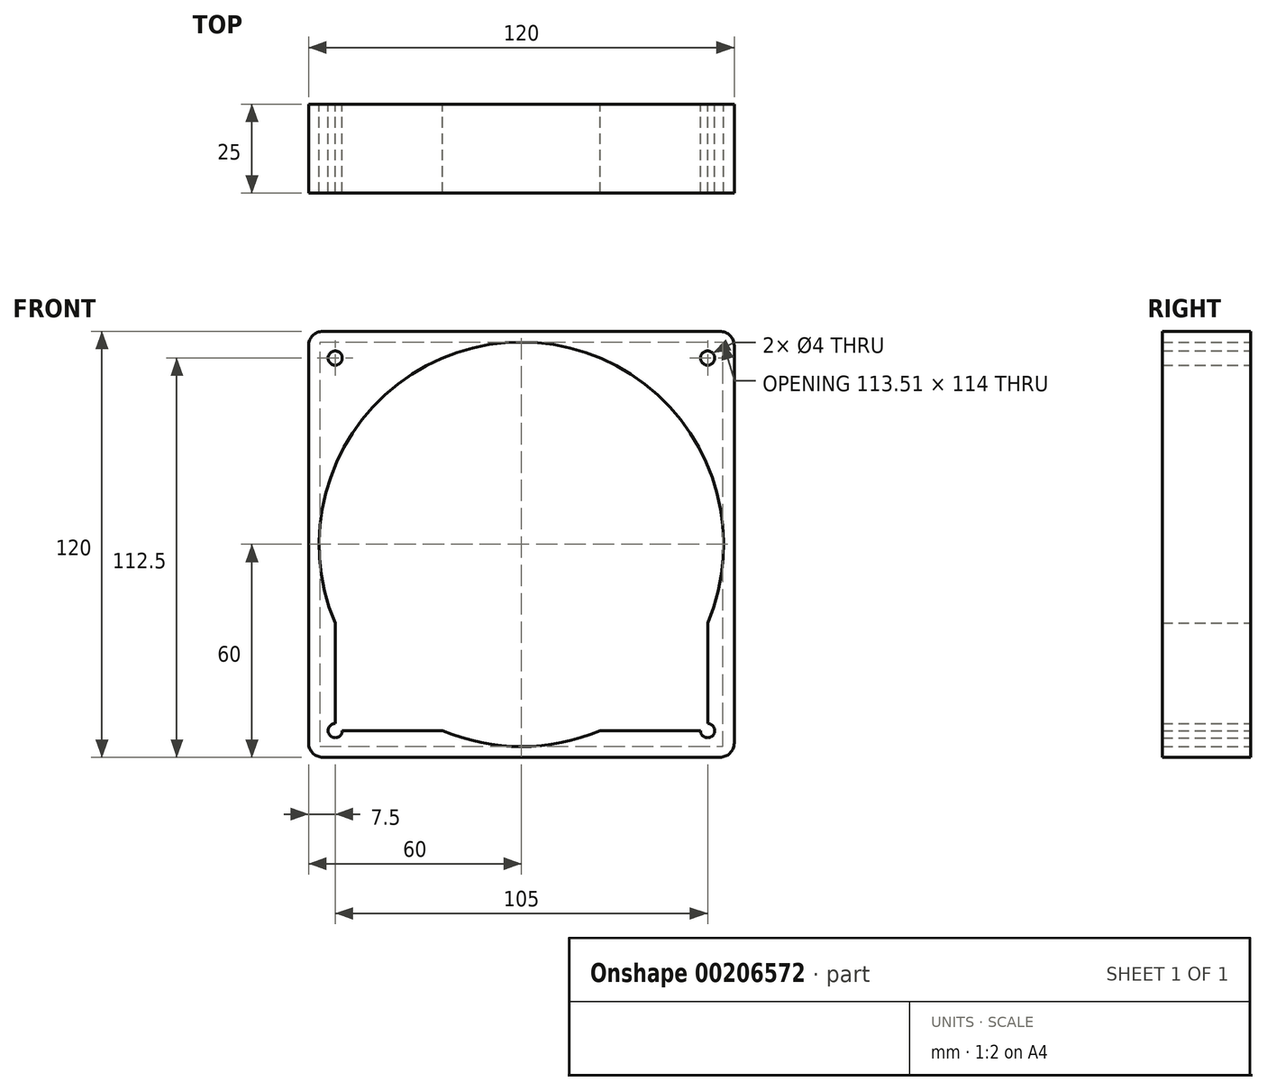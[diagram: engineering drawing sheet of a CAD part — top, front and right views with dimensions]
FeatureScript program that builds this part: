
annotation { "Feature Type Name" : "Feature", "Feature Type Description" : "" }
export const myFeature = defineFeature(function(context is Context, id is Id, definition is map)
    precondition{}
    {
        {
            var Q0;
            Q0=qCreatedBy(makeId("Front.planeOp"),FACE);
            var sketch = newSketch(context, id + "F0", { "sketchPlane" : qUnion([Q0])});
            skLineSegment(sketch, "E0.bottom", {"start": v(56, -60) * mm, "end": v(-56, -60) * mm});
            skLineSegment(sketch, "E0.top", {"start": v(56, 60) * mm, "end": v(-56, 60) * mm});
            skLineSegment(sketch, "E0.left", {"start": v(60, -56) * mm, "end": v(60, 56) * mm});
            skLineSegment(sketch, "E0.right", {"start": v(-60, -56) * mm, "end": v(-60, 56) * mm});
            skPoint(sketch, "E0.middle", {"position": v(0, 0) * mm});
            skCircle(sketch, "E1", {"center": v(0, 0) * mm, "radius": 57 * mm});
            skPoint(sketch, "E2.visualSharp", {"position": v(-60, 60) * mm});
            skArc(sketch, "E2.filletArc", {"start": v(-56, 60) * mm, "mid": v(-58.83, 58.83) * mm, "end": v(-60, 56) * mm});
            skPoint(sketch, "E3.visualSharp", {"position": v(60, 60) * mm});
            skArc(sketch, "E3.filletArc", {"start": v(60, 56) * mm, "mid": v(58.83, 58.83) * mm, "end": v(56, 60) * mm});
            skPoint(sketch, "E4.visualSharp", {"position": v(60, -60) * mm});
            skArc(sketch, "E4.filletArc", {"start": v(56, -60) * mm, "mid": v(58.83, -58.83) * mm, "end": v(60, -56) * mm});
            skPoint(sketch, "E5.visualSharp", {"position": v(-60, -60) * mm});
            skArc(sketch, "E5.filletArc", {"start": v(-60, -56) * mm, "mid": v(-58.83, -58.83) * mm, "end": v(-56, -60) * mm});
            skLineSegment(sketch, "E6.bottom", {"start": v(52.5, -52.5) * mm, "end": v(-52.5, -52.5) * mm});
            skLineSegment(sketch, "E6.top", {"start": v(52.5, 52.5) * mm, "end": v(-52.5, 52.5) * mm});
            skLineSegment(sketch, "E6.left", {"start": v(52.5, -52.5) * mm, "end": v(52.5, 52.5) * mm});
            skLineSegment(sketch, "E6.right", {"start": v(-52.5, -52.5) * mm, "end": v(-52.5, 52.5) * mm});
            skCircle(sketch, "E7", {"center": v(-52.5, 52.5) * mm, "radius": 2 * mm});
            skCircle(sketch, "E8", {"center": v(-52.5, -52.5) * mm, "radius": 2 * mm});
            skCircle(sketch, "E9", {"center": v(52.5, -52.5) * mm, "radius": 2 * mm});
            skCircle(sketch, "E10", {"center": v(52.5, 52.5) * mm, "radius": 2 * mm});
            skSolve(sketch);
        }
        {
            var Q0;
            Q0=makeQuery(id+"F0.imprint","IMPRINT",FACE,{"disambiguationData":[TD([[makeQuery(id+"F0.imprint","IMPRINT",EDGE,{"derivedFrom":sQuery(id+"F0.wireOp",EDGE,"E0.bottom")}),-1.0]])]});
            var Q1;
            {var subQ0=sQuery(id+"F0.wireOp",EDGE,"E6.top");var subQ1=sQuery(id+"F0.wireOp",EDGE,"E1");var subQ2=makeQuery(id+"F0.imprint","INTERSECT",VERTEX,{"disambiguationData":[OD(1.0)],"derivedFrom":[subQ1,subQ0]});Q1=makeQuery(id+"F0.imprint","IMPRINT",FACE,{"disambiguationData":[TD([[makeQuery(id+"F0.imprint","IMPRINT",EDGE,{"disambiguationData":[TD([[subQ2,-1.0]])],"derivedFrom":subQ1}),-1.0]])]});}
            var Q2;
            {var subQ0=sQuery(id+"F0.wireOp",EDGE,"E6.top");var subQ1=sQuery(id+"F0.wireOp",EDGE,"E1");var subQ2=makeQuery(id+"F0.imprint","INTERSECT",VERTEX,{"disambiguationData":[OD(0.0)],"derivedFrom":[subQ1,subQ0]});Q2=makeQuery(id+"F0.imprint","IMPRINT",FACE,{"disambiguationData":[TD([[makeQuery(id+"F0.imprint","IMPRINT",EDGE,{"disambiguationData":[TD([[subQ2,1.0]])],"derivedFrom":subQ1}),-1.0]])]});}
            var Q3;
            {var subQ0=sQuery(id+"F0.wireOp",EDGE,"E6.bottom");var subQ1=sQuery(id+"F0.wireOp",EDGE,"E1");var subQ2=makeQuery(id+"F0.imprint","INTERSECT",VERTEX,{"disambiguationData":[OD(1.0)],"derivedFrom":[subQ1,subQ0]});Q3=makeQuery(id+"F0.imprint","IMPRINT",FACE,{"disambiguationData":[TD([[makeQuery(id+"F0.imprint","IMPRINT",EDGE,{"disambiguationData":[TD([[subQ2,-1.0]])],"derivedFrom":subQ1}),-1.0]])]});}
            var Q4;
            {var subQ0=sQuery(id+"F0.wireOp",EDGE,"E6.right");var subQ1=sQuery(id+"F0.wireOp",EDGE,"E1");var subQ2=makeQuery(id+"F0.imprint","INTERSECT",VERTEX,{"disambiguationData":[OD(1.0)],"derivedFrom":[subQ1,subQ0]});Q4=makeQuery(id+"F0.imprint","IMPRINT",FACE,{"disambiguationData":[TD([[makeQuery(id+"F0.imprint","IMPRINT",EDGE,{"disambiguationData":[TD([[subQ2,-1.0]])],"derivedFrom":subQ1}),-1.0]])]});}
            extrude(context, id + "F1", {"entities" : qUnion([Q0, Q1, Q2, Q3, Q4]), "depth" : 25 * mm});
        }
    });
